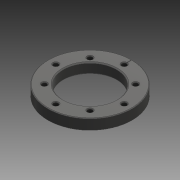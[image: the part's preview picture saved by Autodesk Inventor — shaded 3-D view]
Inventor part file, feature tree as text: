
AUTODESK INVENTOR PART (.ipt)
format: ipt  version: 2023 (Build 270158000, 158)  size: 190,976 bytes
history: native  units: mm
features: other x1, extrude x1, sketch x1, imported_body x1
ambient origin geometry x8: Origin, YZ Plane, XZ Plane, XY Plane, X Axis, Y Axis, Z Axis, Center Point
bodies: Body1 (feature_tree)
feature tree (4):
  other  "ソリッド1"
  extrude  "押し出し1"  TaperAngle=0.0deg  [1 undecoded]
  sketch  "スケッチ1"
  imported_body  "Base1"
note: 1 required parameter value undecoded (feature->parameter linkage not recoverable at this tier; creation-order binding heuristic only, values carry confidence <= 0.55)
